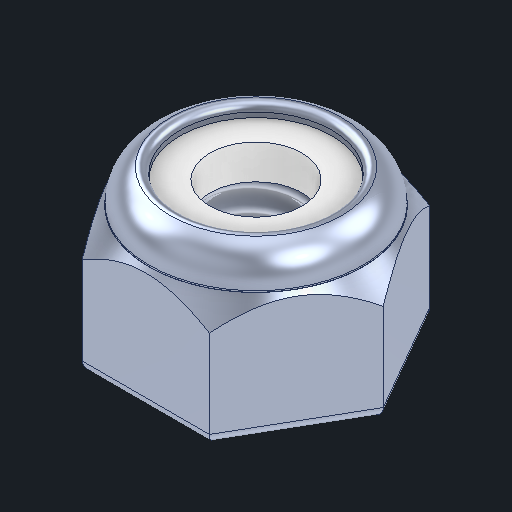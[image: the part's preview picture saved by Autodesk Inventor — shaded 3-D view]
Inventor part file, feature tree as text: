
AUTODESK INVENTOR PART (.ipt)
format: ipt  version: 2024 (Build 280153000, 153)  size: 225,280 bytes
history: native  units: in
note: dims shown in document units (in); Inventor stores cm internally (conversion verified against a paired STEP export)
features: other x4, plane x2, sketch x1
ambient origin geometry x8: Origin, YZ Plane, XZ Plane, XY Plane, X Axis, Y Axis, Z Axis, Center Point
bodies: Body1 (feature_tree)
feature tree (7):
  other  "Nut Nylock.ipt"
  other  "NONE::Nut Nylock.ipt"
  other  "TaggingFeature1"
  sketch  "Sketch1"  dims[d0=0.3937in]
  plane  "Work Plane1"
  plane  "Work Plane2"
  parser-record x1  (decoder bookkeeping rows leaked as tree rows — omitted from the tree; the rows remain in map.json)
